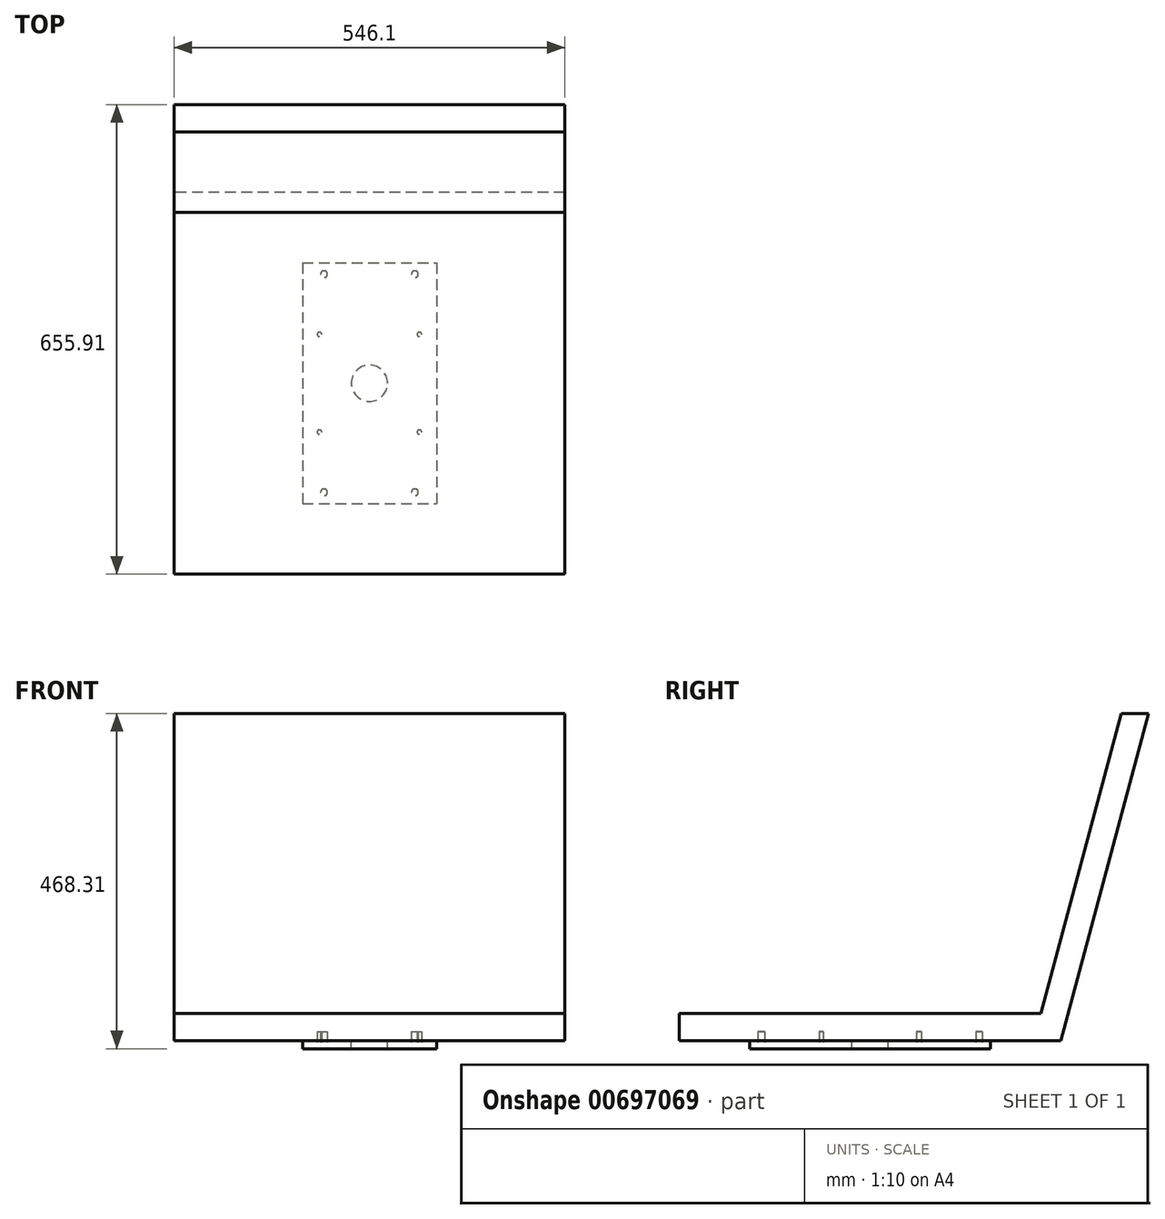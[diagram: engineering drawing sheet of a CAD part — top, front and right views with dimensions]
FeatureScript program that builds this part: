
annotation { "Feature Type Name" : "Feature", "Feature Type Description" : "" }
export const myFeature = defineFeature(function(context is Context, id is Id, definition is map)
    precondition{}
    {
        {
            var Q0;
            Q0=qCreatedBy(makeId("Right.planeOp"),FACE);
            var sketch = newSketch(context, id + "F0", { "sketchPlane" : qUnion([Q0])});
            skLineSegment(sketch, "E0", {"start": v(0, 0) * mm, "end": v(533.4, 0) * mm});
            skLineSegment(sketch, "E1", {"start": v(533.4, 0) * mm, "end": v(655.9, 457.2) * mm});
            skLineSegment(sketch, "E2", {"start": v(0, 0) * mm, "end": v(0, 38.1) * mm});
            skLineSegment(sketch, "E3", {"start": v(0, 38.1) * mm, "end": v(505.5, 38.1) * mm});
            skLineSegment(sketch, "E4", {"start": v(505.5, 38.1) * mm, "end": v(617.8, 457.2) * mm});
            skLineSegment(sketch, "E5", {"start": v(617.8, 457.2) * mm, "end": v(655.9, 457.2) * mm});
            skSolve(sketch);
        }
        {
            var Q0;
            Q0 = qSketchRegion(id + "F0", true);
            extrude(context, id + "F1", {"entities" : qUnion([Q0]), "depth" : 273.05 * mm, "offsetDistance" : 25.4 * mm, "hasSecondDirection" : true, "secondDirectionOppositeDirection" : true, "secondDirectionDepth" : 273.05 * mm});
        }
        {
            var Q0;
            Q0=makeQuery(id+"F1.opExtrude","SWEPT_FACE",FACE,{"disambiguationData":[OSD([sQuery(id+"F0.wireOp",EDGE,"E0")])]});
            var sketch = newSketch(context, id + "F2", { "sketchPlane" : qUnion([Q0])});
            skLineSegment(sketch, "E6.bottom", {"start": v(-63.5, -419.1) * mm, "end": v(63.5, -419.1) * mm, "construction": true});
            skLineSegment(sketch, "E6.top", {"start": v(-63.5, -114.3) * mm, "end": v(63.5, -114.3) * mm, "construction": true});
            skLineSegment(sketch, "E6.left", {"start": v(-63.5, -419.1) * mm, "end": v(-63.5, -114.3) * mm, "construction": true});
            skLineSegment(sketch, "E6.right", {"start": v(63.5, -419.1) * mm, "end": v(63.5, -114.3) * mm, "construction": true});
            skPoint(sketch, "E6.middle", {"position": v(0, -266.7) * mm});
            skCircle(sketch, "E7", {"center": v(-63.5, -114.3) * mm, "radius": 4.76 * mm});
            skCircle(sketch, "E8", {"center": v(-63.5, -419.1) * mm, "radius": 4.76 * mm});
            skCircle(sketch, "E9", {"center": v(63.5, -419.1) * mm, "radius": 4.76 * mm});
            skLineSegment(sketch, "E10", {"start": v(-273.05, -266.7) * mm, "end": v(0, -266.7) * mm, "construction": true});
            skLineSegment(sketch, "E11", {"start": v(69.85, -198.44) * mm, "end": v(69.85, -334.96) * mm, "construction": true});
            skLineSegment(sketch, "E12", {"start": v(-69.85, -198.44) * mm, "end": v(-69.85, -334.96) * mm, "construction": true});
            skCircle(sketch, "E13", {"center": v(69.85, -334.96) * mm, "radius": 3.18 * mm});
            skCircle(sketch, "E14", {"center": v(69.85, -198.44) * mm, "radius": 3.18 * mm});
            skCircle(sketch, "E15", {"center": v(-69.85, -198.44) * mm, "radius": 3.18 * mm});
            skCircle(sketch, "E16", {"center": v(-69.85, -334.96) * mm, "radius": 3.18 * mm});
            skLineSegment(sketch, "E17", {"start": v(0, -198.44) * mm, "end": v(0, -266.7) * mm, "construction": true});
            skLineSegment(sketch, "E18", {"start": v(0, -266.7) * mm, "end": v(69.85, -266.7) * mm, "construction": true});
            skLineSegment(sketch, "E19", {"start": v(69.85, -334.96) * mm, "end": v(-69.85, -334.96) * mm, "construction": true});
            skLineSegment(sketch, "E20", {"start": v(69.85, -198.44) * mm, "end": v(-69.85, -198.44) * mm, "construction": true});
            skLineSegment(sketch, "E21", {"start": v(0, -266.7) * mm, "end": v(0, -334.96) * mm, "construction": true});
            skCircle(sketch, "E22", {"center": v(63.5, -114.3) * mm, "radius": 4.76 * mm});
            skSolve(sketch);
        }
        {
            var Q0;
            Q0 = qSketchRegion(id + "F2", true);
            extrude(context, id + "F3", {"entities" : qUnion([Q0]), "operationType" : NewBodyOperationType.REMOVE, "oppositeDirection" : true, "depth" : 12.7 * mm, "offsetDistance" : 25.4 * mm});
        }
        {
            var Q0;
            Q0=makeQuery(id+"F1.opExtrude","SWEPT_FACE",FACE,{"disambiguationData":[OSD([sQuery(id+"F0.wireOp",EDGE,"E0")])]});
            var sketch = newSketch(context, id + "F4", { "sketchPlane" : qUnion([Q0])});
            skLineSegment(sketch, "E23.bottom", {"start": v(-93.66, -434.98) * mm, "end": v(93.66, -434.98) * mm});
            skLineSegment(sketch, "E23.top", {"start": v(-93.66, -98.43) * mm, "end": v(93.66, -98.43) * mm});
            skLineSegment(sketch, "E23.left", {"start": v(-93.66, -434.98) * mm, "end": v(-93.66, -98.43) * mm});
            skLineSegment(sketch, "E23.right", {"start": v(93.66, -434.98) * mm, "end": v(93.66, -98.43) * mm});
            skPoint(sketch, "E23.middle", {"position": v(0, -266.7) * mm});
            skCircle(sketch, "E24.0", {"center": v(63.5, -114.3) * mm, "radius": 4.76 * mm});
            skCircle(sketch, "E25.0", {"center": v(69.85, -198.44) * mm, "radius": 3.18 * mm});
            skCircle(sketch, "E26.0", {"center": v(-63.5, -114.3) * mm, "radius": 4.76 * mm});
            skCircle(sketch, "E27.0", {"center": v(-69.85, -198.44) * mm, "radius": 3.18 * mm});
            skCircle(sketch, "E28.0", {"center": v(-69.85, -334.96) * mm, "radius": 3.18 * mm});
            skCircle(sketch, "E29.0", {"center": v(-63.5, -419.1) * mm, "radius": 4.76 * mm});
            skCircle(sketch, "E30.0", {"center": v(63.5, -419.1) * mm, "radius": 4.76 * mm});
            skCircle(sketch, "E31.0", {"center": v(69.85, -334.96) * mm, "radius": 3.18 * mm});
            skCircle(sketch, "E32", {"center": v(0, -266.7) * mm, "radius": 25.4 * mm});
            skSolve(sketch);
        }
        {
            var Q0;
            Q0 = qSketchRegion(id + "F4", true);
            extrude(context, id + "F5", {"entities" : qUnion([Q0]), "operationType" : NewBodyOperationType.ADD, "depth" : 11.1 * mm, "offsetDistance" : 25.4 * mm});
        }
    });
